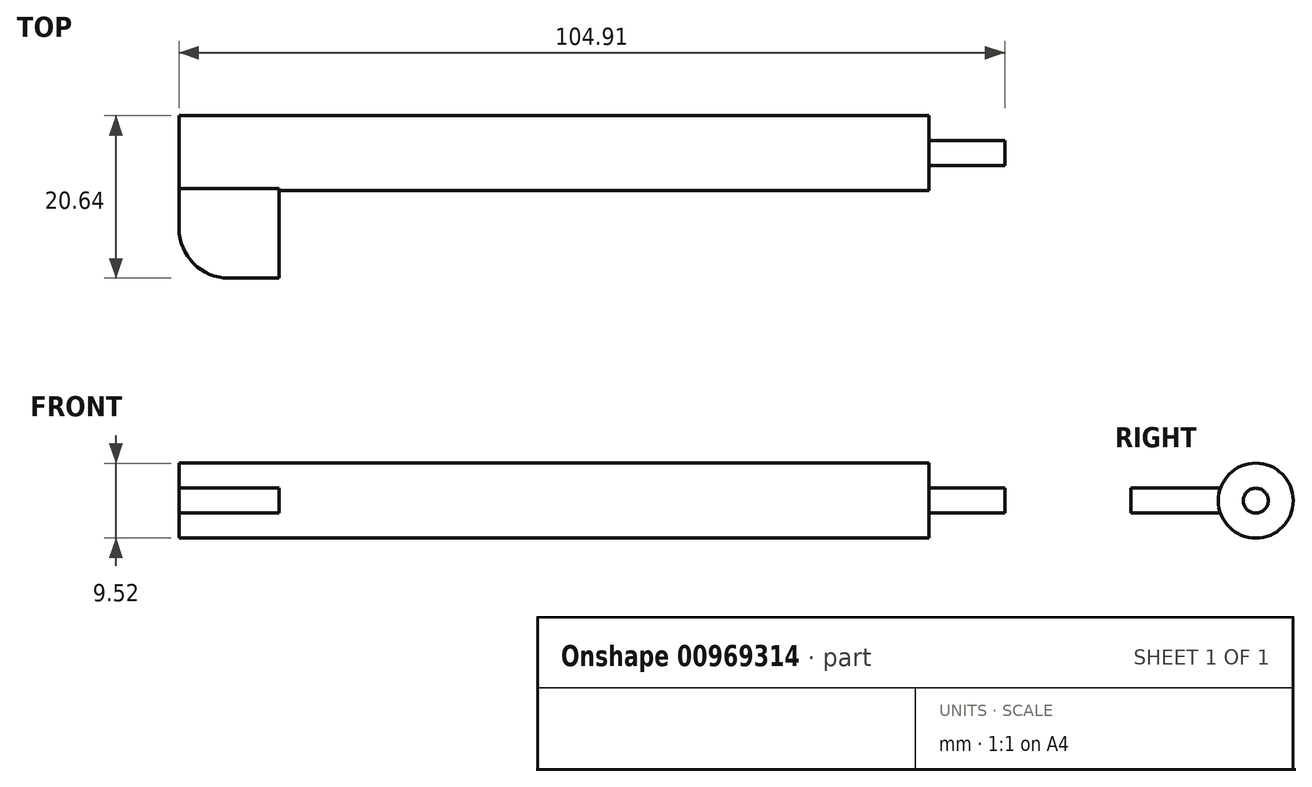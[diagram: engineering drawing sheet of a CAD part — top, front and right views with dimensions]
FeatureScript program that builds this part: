
annotation { "Feature Type Name" : "Feature", "Feature Type Description" : "" }
export const myFeature = defineFeature(function(context is Context, id is Id, definition is map)
    precondition{}
    {
        {
            var Q0;
            Q0=qCreatedBy(makeId("Top.planeOp"),FACE);
            var sketch = newSketch(context, id + "F0", { "sketchPlane" : qUnion([Q0])});
            skLineSegment(sketch, "E0.bottom", {"start": v(-44.65, 32.5) * mm, "end": v(37.9, 32.5) * mm});
            skLineSegment(sketch, "E0.top", {"start": v(-44.65, 22.97) * mm, "end": v(37.9, 22.97) * mm});
            skLineSegment(sketch, "E0.left", {"start": v(-44.65, 32.5) * mm, "end": v(-44.65, 22.97) * mm});
            skLineSegment(sketch, "E1", {"start": v(47.56, 27.74) * mm, "end": v(47.56, 29.32) * mm});
            skLineSegment(sketch, "E2", {"start": v(47.56, 29.32) * mm, "end": v(37.9, 29.32) * mm});
            skLineSegment(sketch, "E3", {"start": v(47.56, 27.74) * mm, "end": v(47.56, 26.15) * mm});
            skLineSegment(sketch, "E4", {"start": v(47.56, 26.15) * mm, "end": v(37.9, 26.15) * mm});
            skLineSegment(sketch, "E5", {"start": v(37.9, 32.5) * mm, "end": v(37.9, 29.32) * mm});
            skLineSegment(sketch, "E6", {"start": v(37.9, 22.97) * mm, "end": v(37.9, 26.15) * mm});
            skLineSegment(sketch, "E7.bottom", {"start": v(-44.65, 32.5) * mm, "end": v(-57.35, 32.5) * mm});
            skLineSegment(sketch, "E7.top", {"start": v(-44.65, 11.86) * mm, "end": v(-57.35, 11.86) * mm});
            skLineSegment(sketch, "E7.left", {"start": v(-44.65, 32.5) * mm, "end": v(-44.65, 11.86) * mm});
            skLineSegment(sketch, "E7.right", {"start": v(-57.35, 32.5) * mm, "end": v(-57.35, 11.86) * mm});
            skLineSegment(sketch, "E8", {"start": v(47.56, 27.74) * mm, "end": v(-44.65, 27.74) * mm});
            skLineSegment(sketch, "E9", {"start": v(-44.65, 27.74) * mm, "end": v(-57.35, 27.74) * mm});
            skSolve(sketch);
        }
        {
            var Q0;
            {var subQ0=sQuery(id+"F0.wireOp",EDGE,"E7.bottom");Q0=makeQuery(id+"F0.imprint","IMPRINT",FACE,{"disambiguationData":[TD([[makeQuery(id+"F0.imprint","IMPRINT",EDGE,{"derivedFrom":subQ0}),1.0]])]});}
            var Q1;
            {var subQ0=sQuery(id+"F0.wireOp",EDGE,"E0.bottom");Q1=makeQuery(id+"F0.imprint","IMPRINT",FACE,{"disambiguationData":[TD([[makeQuery(id+"F0.imprint","IMPRINT",EDGE,{"derivedFrom":subQ0}),-1.0]])]});}
            var Q2;
            Q2=sQuery(id+"F0.wireOp",EDGE,"E8");
            revolve(context, id + "F1", {"surfaceOperationType" : NewSurfaceOperationType.NEW, "entities" : qUnion([Q0, Q1]), "axis" : qUnion([Q2]), "revolveType" : RevolveType.FULL});
        }
        {
            var Q0;
            {var subQ2=sQuery(id+"F0.wireOp",EDGE,"E7.top");Q0=makeQuery(id+"F0.imprint","IMPRINT",FACE,{"disambiguationData":[TD([[makeQuery(id+"F0.imprint","IMPRINT",EDGE,{"derivedFrom":subQ2}),-1.0]])]});}
            extrude(context, id + "F2", {"entities" : qUnion([Q0]), "operationType" : NewBodyOperationType.ADD, "endBound" : BoundingType.SYMMETRIC, "depth" : 3.17 * mm, "offsetDistance" : 25.4 * mm});
        }
        {
            var Q0;
            Q0=makeQuery(id+"F2.opExtrude","SWEPT_EDGE",EDGE,{"disambiguationData":[OSD([sQuery(id+"F0.wireOp",EDGE,"E7.top"),sQuery(id+"F0.wireOp",EDGE,"E7.right")])]});
            fillet(context, id + "F3", {"entities" : qUnion([Q0]), "radius" : 6.35 * mm, "tangentPropagation" : true, "allowEdgeOverflow" : false});
        }
    });
